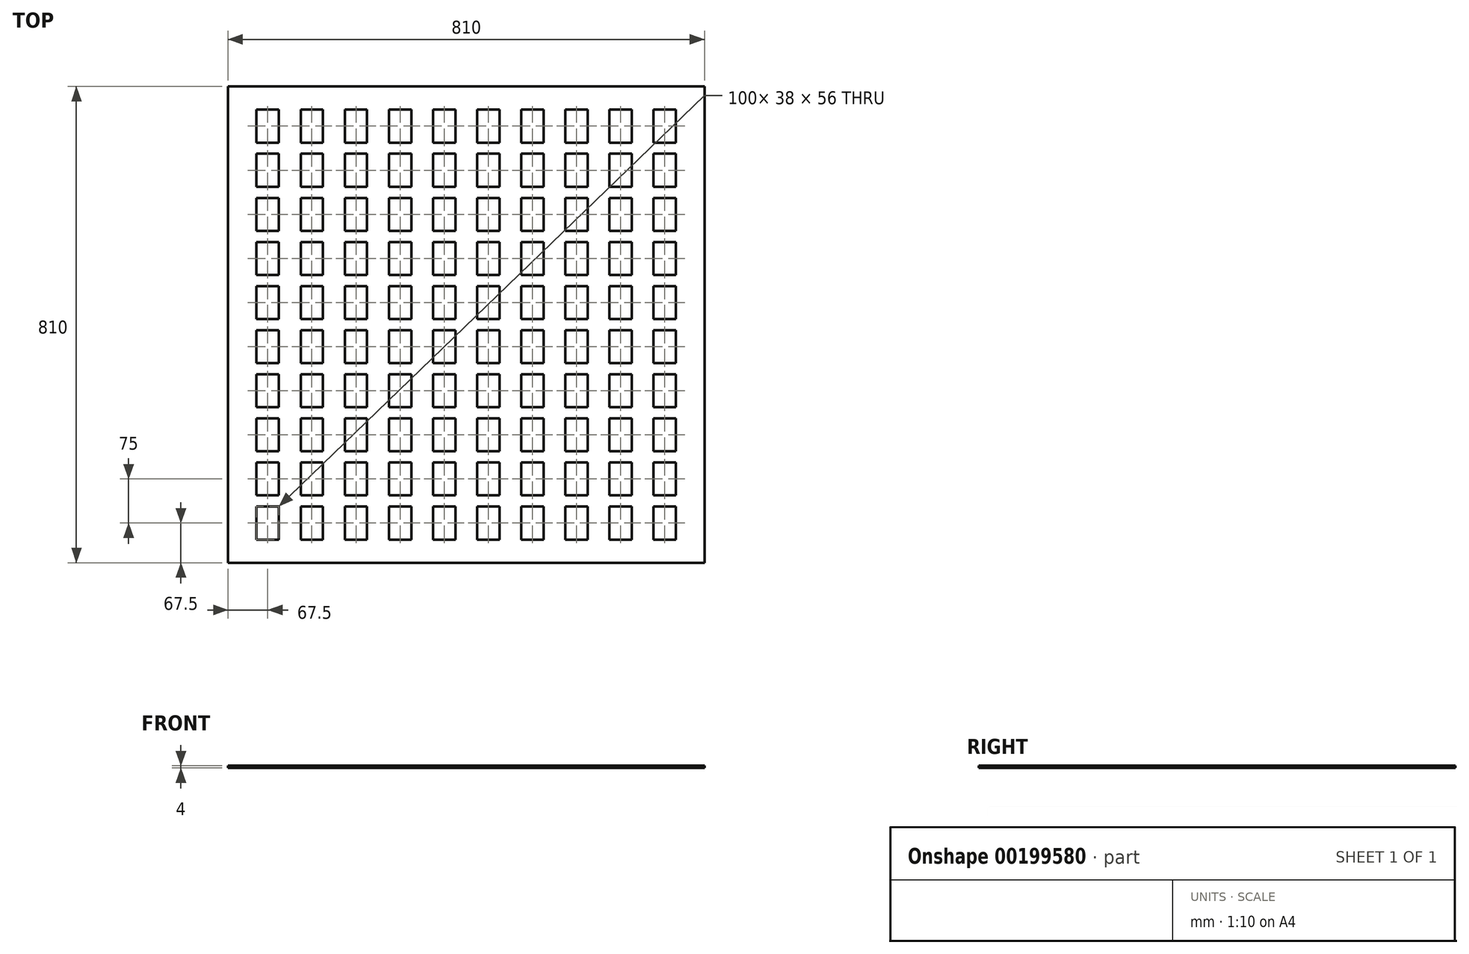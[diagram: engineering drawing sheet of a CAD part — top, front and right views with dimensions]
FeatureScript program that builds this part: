
annotation { "Feature Type Name" : "Feature", "Feature Type Description" : "" }
export const myFeature = defineFeature(function(context is Context, id is Id, definition is map)
    precondition{}
    {
        {
            var Q0;
            Q0=qCreatedBy(makeId("Top.planeOp"),FACE);
            var sketch = newSketch(context, id + "F0", { "sketchPlane" : qUnion([Q0])});
            skLineSegment(sketch, "E0.bottom", {"start": v(-405, 405) * mm, "end": v(405, 405) * mm});
            skLineSegment(sketch, "E0.top", {"start": v(-405, -405) * mm, "end": v(405, -405) * mm});
            skLineSegment(sketch, "E0.left", {"start": v(-405, 405) * mm, "end": v(-405, -405) * mm});
            skLineSegment(sketch, "E0.right", {"start": v(405, 405) * mm, "end": v(405, -405) * mm});
            skSolve(sketch);
        }
        {
            var Q0;
            Q0=makeQuery(id+"F0.imprint","IMPRINT",FACE,{"disambiguationData":[TD([[makeQuery(id+"F0.imprint","IMPRINT",EDGE,{"derivedFrom":sQuery(id+"F0.wireOp",EDGE,"E0.bottom")}),-1.0]])]});
            extrude(context, id + "F1", {"entities" : qUnion([Q0]), "depth" : 4 * mm});
        }
        {
            var Q0;
            Q0=makeQuery(id+"F1.opExtrude","CAP_FACE",FACE,{"disambiguationData":[OSD([sQuery(id+"F0.wireOp",EDGE,"E0.bottom"),sQuery(id+"F0.wireOp",EDGE,"E0.top"),sQuery(id+"F0.wireOp",EDGE,"E0.left"),sQuery(id+"F0.wireOp",EDGE,"E0.right")])],"isStart":false});
            var sketch = newSketch(context, id + "F2", { "sketchPlane" : qUnion([Q0])});
            skCircle(sketch, "E1", {"center": v(-337.5, 337.5) * mm, "radius": 37.5 * mm, "construction": true});
            skLineSegment(sketch, "E2.bottom", {"start": v(-318.5, 309.5) * mm, "end": v(-356.5, 309.5) * mm});
            skLineSegment(sketch, "E2.top", {"start": v(-318.5, 365.5) * mm, "end": v(-356.5, 365.5) * mm});
            skLineSegment(sketch, "E2.left", {"start": v(-318.5, 309.5) * mm, "end": v(-318.5, 365.5) * mm});
            skLineSegment(sketch, "E2.right", {"start": v(-356.5, 309.5) * mm, "end": v(-356.5, 365.5) * mm});
            skLineSegment(sketch, "E3.0.1.0", {"start": v(-318.5, 234.5) * mm, "end": v(-318.5, 290.5) * mm});
            skPoint(sketch, "E3.0.1.1", {"position": v(-337.5, 262.5) * mm});
            skLineSegment(sketch, "E3.0.1.2", {"start": v(-356.5, 234.5) * mm, "end": v(-356.5, 290.5) * mm});
            skCircle(sketch, "E3.0.1.3", {"center": v(-337.5, 262.5) * mm, "radius": 37.5 * mm, "construction": true});
            skLineSegment(sketch, "E3.0.1.4", {"start": v(-318.5, 234.5) * mm, "end": v(-356.5, 234.5) * mm});
            skLineSegment(sketch, "E3.0.1.5", {"start": v(-318.5, 290.5) * mm, "end": v(-356.5, 290.5) * mm});
            skLineSegment(sketch, "E3.0.2.0", {"start": v(-318.5, 159.5) * mm, "end": v(-318.5, 215.5) * mm});
            skPoint(sketch, "E3.0.2.1", {"position": v(-337.5, 187.5) * mm});
            skLineSegment(sketch, "E3.0.2.2", {"start": v(-356.5, 159.5) * mm, "end": v(-356.5, 215.5) * mm});
            skCircle(sketch, "E3.0.2.3", {"center": v(-337.5, 187.5) * mm, "radius": 37.5 * mm, "construction": true});
            skLineSegment(sketch, "E3.0.2.4", {"start": v(-318.5, 159.5) * mm, "end": v(-356.5, 159.5) * mm});
            skLineSegment(sketch, "E3.0.2.5", {"start": v(-318.5, 215.5) * mm, "end": v(-356.5, 215.5) * mm});
            skLineSegment(sketch, "E3.0.3.0", {"start": v(-318.5, 84.5) * mm, "end": v(-318.5, 140.5) * mm});
            skPoint(sketch, "E3.0.3.1", {"position": v(-337.5, 112.5) * mm});
            skLineSegment(sketch, "E3.0.3.2", {"start": v(-356.5, 84.5) * mm, "end": v(-356.5, 140.5) * mm});
            skCircle(sketch, "E3.0.3.3", {"center": v(-337.5, 112.5) * mm, "radius": 37.5 * mm, "construction": true});
            skLineSegment(sketch, "E3.0.3.4", {"start": v(-318.5, 84.5) * mm, "end": v(-356.5, 84.5) * mm});
            skLineSegment(sketch, "E3.0.3.5", {"start": v(-318.5, 140.5) * mm, "end": v(-356.5, 140.5) * mm});
            skLineSegment(sketch, "E3.0.4.0", {"start": v(-318.5, 9.5) * mm, "end": v(-318.5, 65.5) * mm});
            skPoint(sketch, "E3.0.4.1", {"position": v(-337.5, 37.5) * mm});
            skLineSegment(sketch, "E3.0.4.2", {"start": v(-356.5, 9.5) * mm, "end": v(-356.5, 65.5) * mm});
            skCircle(sketch, "E3.0.4.3", {"center": v(-337.5, 37.5) * mm, "radius": 37.5 * mm, "construction": true});
            skLineSegment(sketch, "E3.0.4.4", {"start": v(-318.5, 9.5) * mm, "end": v(-356.5, 9.5) * mm});
            skLineSegment(sketch, "E3.0.4.5", {"start": v(-318.5, 65.5) * mm, "end": v(-356.5, 65.5) * mm});
            skLineSegment(sketch, "E3.0.5.0", {"start": v(-318.5, -65.5) * mm, "end": v(-318.5, -9.5) * mm});
            skPoint(sketch, "E3.0.5.1", {"position": v(-337.5, -37.5) * mm});
            skLineSegment(sketch, "E3.0.5.2", {"start": v(-356.5, -65.5) * mm, "end": v(-356.5, -9.5) * mm});
            skCircle(sketch, "E3.0.5.3", {"center": v(-337.5, -37.5) * mm, "radius": 37.5 * mm, "construction": true});
            skLineSegment(sketch, "E3.0.5.4", {"start": v(-318.5, -65.5) * mm, "end": v(-356.5, -65.5) * mm});
            skLineSegment(sketch, "E3.0.5.5", {"start": v(-318.5, -9.5) * mm, "end": v(-356.5, -9.5) * mm});
            skLineSegment(sketch, "E3.0.6.0", {"start": v(-318.5, -140.5) * mm, "end": v(-318.5, -84.5) * mm});
            skPoint(sketch, "E3.0.6.1", {"position": v(-337.5, -112.5) * mm});
            skLineSegment(sketch, "E3.0.6.2", {"start": v(-356.5, -140.5) * mm, "end": v(-356.5, -84.5) * mm});
            skCircle(sketch, "E3.0.6.3", {"center": v(-337.5, -112.5) * mm, "radius": 37.5 * mm, "construction": true});
            skLineSegment(sketch, "E3.0.6.4", {"start": v(-318.5, -140.5) * mm, "end": v(-356.5, -140.5) * mm});
            skLineSegment(sketch, "E3.0.6.5", {"start": v(-318.5, -84.5) * mm, "end": v(-356.5, -84.5) * mm});
            skLineSegment(sketch, "E3.0.7.0", {"start": v(-318.5, -215.5) * mm, "end": v(-318.5, -159.5) * mm});
            skPoint(sketch, "E3.0.7.1", {"position": v(-337.5, -187.5) * mm});
            skLineSegment(sketch, "E3.0.7.2", {"start": v(-356.5, -215.5) * mm, "end": v(-356.5, -159.5) * mm});
            skCircle(sketch, "E3.0.7.3", {"center": v(-337.5, -187.5) * mm, "radius": 37.5 * mm, "construction": true});
            skLineSegment(sketch, "E3.0.7.4", {"start": v(-318.5, -215.5) * mm, "end": v(-356.5, -215.5) * mm});
            skLineSegment(sketch, "E3.0.7.5", {"start": v(-318.5, -159.5) * mm, "end": v(-356.5, -159.5) * mm});
            skLineSegment(sketch, "E3.0.8.0", {"start": v(-318.5, -290.5) * mm, "end": v(-318.5, -234.5) * mm});
            skPoint(sketch, "E3.0.8.1", {"position": v(-337.5, -262.5) * mm});
            skLineSegment(sketch, "E3.0.8.2", {"start": v(-356.5, -290.5) * mm, "end": v(-356.5, -234.5) * mm});
            skCircle(sketch, "E3.0.8.3", {"center": v(-337.5, -262.5) * mm, "radius": 37.5 * mm, "construction": true});
            skLineSegment(sketch, "E3.0.8.4", {"start": v(-318.5, -290.5) * mm, "end": v(-356.5, -290.5) * mm});
            skLineSegment(sketch, "E3.0.8.5", {"start": v(-318.5, -234.5) * mm, "end": v(-356.5, -234.5) * mm});
            skLineSegment(sketch, "E3.0.9.0", {"start": v(-318.5, -365.5) * mm, "end": v(-318.5, -309.5) * mm});
            skPoint(sketch, "E3.0.9.1", {"position": v(-337.5, -337.5) * mm});
            skLineSegment(sketch, "E3.0.9.2", {"start": v(-356.5, -365.5) * mm, "end": v(-356.5, -309.5) * mm});
            skCircle(sketch, "E3.0.9.3", {"center": v(-337.5, -337.5) * mm, "radius": 37.5 * mm, "construction": true});
            skLineSegment(sketch, "E3.0.9.4", {"start": v(-318.5, -365.5) * mm, "end": v(-356.5, -365.5) * mm});
            skLineSegment(sketch, "E3.0.9.5", {"start": v(-318.5, -309.5) * mm, "end": v(-356.5, -309.5) * mm});
            skLineSegment(sketch, "E3.1.0.0", {"start": v(-243.5, 309.5) * mm, "end": v(-243.5, 365.5) * mm});
            skPoint(sketch, "E3.1.0.1", {"position": v(-262.5, 337.5) * mm});
            skLineSegment(sketch, "E3.1.0.2", {"start": v(-281.5, 309.5) * mm, "end": v(-281.5, 365.5) * mm});
            skCircle(sketch, "E3.1.0.3", {"center": v(-262.5, 337.5) * mm, "radius": 37.5 * mm, "construction": true});
            skLineSegment(sketch, "E3.1.0.4", {"start": v(-243.5, 309.5) * mm, "end": v(-281.5, 309.5) * mm});
            skLineSegment(sketch, "E3.1.0.5", {"start": v(-243.5, 365.5) * mm, "end": v(-281.5, 365.5) * mm});
            skLineSegment(sketch, "E3.1.1.0", {"start": v(-243.5, 234.5) * mm, "end": v(-243.5, 290.5) * mm});
            skPoint(sketch, "E3.1.1.1", {"position": v(-262.5, 262.5) * mm});
            skLineSegment(sketch, "E3.1.1.2", {"start": v(-281.5, 234.5) * mm, "end": v(-281.5, 290.5) * mm});
            skCircle(sketch, "E3.1.1.3", {"center": v(-262.5, 262.5) * mm, "radius": 37.5 * mm, "construction": true});
            skLineSegment(sketch, "E3.1.1.4", {"start": v(-243.5, 234.5) * mm, "end": v(-281.5, 234.5) * mm});
            skLineSegment(sketch, "E3.1.1.5", {"start": v(-243.5, 290.5) * mm, "end": v(-281.5, 290.5) * mm});
            skLineSegment(sketch, "E3.1.2.0", {"start": v(-243.5, 159.5) * mm, "end": v(-243.5, 215.5) * mm});
            skPoint(sketch, "E3.1.2.1", {"position": v(-262.5, 187.5) * mm});
            skLineSegment(sketch, "E3.1.2.2", {"start": v(-281.5, 159.5) * mm, "end": v(-281.5, 215.5) * mm});
            skCircle(sketch, "E3.1.2.3", {"center": v(-262.5, 187.5) * mm, "radius": 37.5 * mm, "construction": true});
            skLineSegment(sketch, "E3.1.2.4", {"start": v(-243.5, 159.5) * mm, "end": v(-281.5, 159.5) * mm});
            skLineSegment(sketch, "E3.1.2.5", {"start": v(-243.5, 215.5) * mm, "end": v(-281.5, 215.5) * mm});
            skLineSegment(sketch, "E3.1.3.0", {"start": v(-243.5, 84.5) * mm, "end": v(-243.5, 140.5) * mm});
            skPoint(sketch, "E3.1.3.1", {"position": v(-262.5, 112.5) * mm});
            skLineSegment(sketch, "E3.1.3.2", {"start": v(-281.5, 84.5) * mm, "end": v(-281.5, 140.5) * mm});
            skCircle(sketch, "E3.1.3.3", {"center": v(-262.5, 112.5) * mm, "radius": 37.5 * mm, "construction": true});
            skLineSegment(sketch, "E3.1.3.4", {"start": v(-243.5, 84.5) * mm, "end": v(-281.5, 84.5) * mm});
            skLineSegment(sketch, "E3.1.3.5", {"start": v(-243.5, 140.5) * mm, "end": v(-281.5, 140.5) * mm});
            skLineSegment(sketch, "E3.1.4.0", {"start": v(-243.5, 9.5) * mm, "end": v(-243.5, 65.5) * mm});
            skPoint(sketch, "E3.1.4.1", {"position": v(-262.5, 37.5) * mm});
            skLineSegment(sketch, "E3.1.4.2", {"start": v(-281.5, 9.5) * mm, "end": v(-281.5, 65.5) * mm});
            skCircle(sketch, "E3.1.4.3", {"center": v(-262.5, 37.5) * mm, "radius": 37.5 * mm, "construction": true});
            skLineSegment(sketch, "E3.1.4.4", {"start": v(-243.5, 9.5) * mm, "end": v(-281.5, 9.5) * mm});
            skLineSegment(sketch, "E3.1.4.5", {"start": v(-243.5, 65.5) * mm, "end": v(-281.5, 65.5) * mm});
            skLineSegment(sketch, "E3.1.5.0", {"start": v(-243.5, -65.5) * mm, "end": v(-243.5, -9.5) * mm});
            skPoint(sketch, "E3.1.5.1", {"position": v(-262.5, -37.5) * mm});
            skLineSegment(sketch, "E3.1.5.2", {"start": v(-281.5, -65.5) * mm, "end": v(-281.5, -9.5) * mm});
            skCircle(sketch, "E3.1.5.3", {"center": v(-262.5, -37.5) * mm, "radius": 37.5 * mm, "construction": true});
            skLineSegment(sketch, "E3.1.5.4", {"start": v(-243.5, -65.5) * mm, "end": v(-281.5, -65.5) * mm});
            skLineSegment(sketch, "E3.1.5.5", {"start": v(-243.5, -9.5) * mm, "end": v(-281.5, -9.5) * mm});
            skLineSegment(sketch, "E3.1.6.0", {"start": v(-243.5, -140.5) * mm, "end": v(-243.5, -84.5) * mm});
            skPoint(sketch, "E3.1.6.1", {"position": v(-262.5, -112.5) * mm});
            skLineSegment(sketch, "E3.1.6.2", {"start": v(-281.5, -140.5) * mm, "end": v(-281.5, -84.5) * mm});
            skCircle(sketch, "E3.1.6.3", {"center": v(-262.5, -112.5) * mm, "radius": 37.5 * mm, "construction": true});
            skLineSegment(sketch, "E3.1.6.4", {"start": v(-243.5, -140.5) * mm, "end": v(-281.5, -140.5) * mm});
            skLineSegment(sketch, "E3.1.6.5", {"start": v(-243.5, -84.5) * mm, "end": v(-281.5, -84.5) * mm});
            skLineSegment(sketch, "E3.1.7.0", {"start": v(-243.5, -215.5) * mm, "end": v(-243.5, -159.5) * mm});
            skPoint(sketch, "E3.1.7.1", {"position": v(-262.5, -187.5) * mm});
            skLineSegment(sketch, "E3.1.7.2", {"start": v(-281.5, -215.5) * mm, "end": v(-281.5, -159.5) * mm});
            skCircle(sketch, "E3.1.7.3", {"center": v(-262.5, -187.5) * mm, "radius": 37.5 * mm, "construction": true});
            skLineSegment(sketch, "E3.1.7.4", {"start": v(-243.5, -215.5) * mm, "end": v(-281.5, -215.5) * mm});
            skLineSegment(sketch, "E3.1.7.5", {"start": v(-243.5, -159.5) * mm, "end": v(-281.5, -159.5) * mm});
            skLineSegment(sketch, "E3.1.8.0", {"start": v(-243.5, -290.5) * mm, "end": v(-243.5, -234.5) * mm});
            skPoint(sketch, "E3.1.8.1", {"position": v(-262.5, -262.5) * mm});
            skLineSegment(sketch, "E3.1.8.2", {"start": v(-281.5, -290.5) * mm, "end": v(-281.5, -234.5) * mm});
            skCircle(sketch, "E3.1.8.3", {"center": v(-262.5, -262.5) * mm, "radius": 37.5 * mm, "construction": true});
            skLineSegment(sketch, "E3.1.8.4", {"start": v(-243.5, -290.5) * mm, "end": v(-281.5, -290.5) * mm});
            skLineSegment(sketch, "E3.1.8.5", {"start": v(-243.5, -234.5) * mm, "end": v(-281.5, -234.5) * mm});
            skLineSegment(sketch, "E3.1.9.0", {"start": v(-243.5, -365.5) * mm, "end": v(-243.5, -309.5) * mm});
            skPoint(sketch, "E3.1.9.1", {"position": v(-262.5, -337.5) * mm});
            skLineSegment(sketch, "E3.1.9.2", {"start": v(-281.5, -365.5) * mm, "end": v(-281.5, -309.5) * mm});
            skCircle(sketch, "E3.1.9.3", {"center": v(-262.5, -337.5) * mm, "radius": 37.5 * mm, "construction": true});
            skLineSegment(sketch, "E3.1.9.4", {"start": v(-243.5, -365.5) * mm, "end": v(-281.5, -365.5) * mm});
            skLineSegment(sketch, "E3.1.9.5", {"start": v(-243.5, -309.5) * mm, "end": v(-281.5, -309.5) * mm});
            skLineSegment(sketch, "E3.2.0.0", {"start": v(-168.5, 309.5) * mm, "end": v(-168.5, 365.5) * mm});
            skPoint(sketch, "E3.2.0.1", {"position": v(-187.5, 337.5) * mm});
            skLineSegment(sketch, "E3.2.0.2", {"start": v(-206.5, 309.5) * mm, "end": v(-206.5, 365.5) * mm});
            skCircle(sketch, "E3.2.0.3", {"center": v(-187.5, 337.5) * mm, "radius": 37.5 * mm, "construction": true});
            skLineSegment(sketch, "E3.2.0.4", {"start": v(-168.5, 309.5) * mm, "end": v(-206.5, 309.5) * mm});
            skLineSegment(sketch, "E3.2.0.5", {"start": v(-168.5, 365.5) * mm, "end": v(-206.5, 365.5) * mm});
            skLineSegment(sketch, "E3.2.1.0", {"start": v(-168.5, 234.5) * mm, "end": v(-168.5, 290.5) * mm});
            skPoint(sketch, "E3.2.1.1", {"position": v(-187.5, 262.5) * mm});
            skLineSegment(sketch, "E3.2.1.2", {"start": v(-206.5, 234.5) * mm, "end": v(-206.5, 290.5) * mm});
            skCircle(sketch, "E3.2.1.3", {"center": v(-187.5, 262.5) * mm, "radius": 37.5 * mm, "construction": true});
            skLineSegment(sketch, "E3.2.1.4", {"start": v(-168.5, 234.5) * mm, "end": v(-206.5, 234.5) * mm});
            skLineSegment(sketch, "E3.2.1.5", {"start": v(-168.5, 290.5) * mm, "end": v(-206.5, 290.5) * mm});
            skLineSegment(sketch, "E3.2.2.0", {"start": v(-168.5, 159.5) * mm, "end": v(-168.5, 215.5) * mm});
            skPoint(sketch, "E3.2.2.1", {"position": v(-187.5, 187.5) * mm});
            skLineSegment(sketch, "E3.2.2.2", {"start": v(-206.5, 159.5) * mm, "end": v(-206.5, 215.5) * mm});
            skCircle(sketch, "E3.2.2.3", {"center": v(-187.5, 187.5) * mm, "radius": 37.5 * mm, "construction": true});
            skLineSegment(sketch, "E3.2.2.4", {"start": v(-168.5, 159.5) * mm, "end": v(-206.5, 159.5) * mm});
            skLineSegment(sketch, "E3.2.2.5", {"start": v(-168.5, 215.5) * mm, "end": v(-206.5, 215.5) * mm});
            skLineSegment(sketch, "E3.2.3.0", {"start": v(-168.5, 84.5) * mm, "end": v(-168.5, 140.5) * mm});
            skPoint(sketch, "E3.2.3.1", {"position": v(-187.5, 112.5) * mm});
            skLineSegment(sketch, "E3.2.3.2", {"start": v(-206.5, 84.5) * mm, "end": v(-206.5, 140.5) * mm});
            skCircle(sketch, "E3.2.3.3", {"center": v(-187.5, 112.5) * mm, "radius": 37.5 * mm, "construction": true});
            skLineSegment(sketch, "E3.2.3.4", {"start": v(-168.5, 84.5) * mm, "end": v(-206.5, 84.5) * mm});
            skLineSegment(sketch, "E3.2.3.5", {"start": v(-168.5, 140.5) * mm, "end": v(-206.5, 140.5) * mm});
            skLineSegment(sketch, "E3.2.4.0", {"start": v(-168.5, 9.5) * mm, "end": v(-168.5, 65.5) * mm});
            skPoint(sketch, "E3.2.4.1", {"position": v(-187.5, 37.5) * mm});
            skLineSegment(sketch, "E3.2.4.2", {"start": v(-206.5, 9.5) * mm, "end": v(-206.5, 65.5) * mm});
            skCircle(sketch, "E3.2.4.3", {"center": v(-187.5, 37.5) * mm, "radius": 37.5 * mm, "construction": true});
            skLineSegment(sketch, "E3.2.4.4", {"start": v(-168.5, 9.5) * mm, "end": v(-206.5, 9.5) * mm});
            skLineSegment(sketch, "E3.2.4.5", {"start": v(-168.5, 65.5) * mm, "end": v(-206.5, 65.5) * mm});
            skLineSegment(sketch, "E3.2.5.0", {"start": v(-168.5, -65.5) * mm, "end": v(-168.5, -9.5) * mm});
            skPoint(sketch, "E3.2.5.1", {"position": v(-187.5, -37.5) * mm});
            skLineSegment(sketch, "E3.2.5.2", {"start": v(-206.5, -65.5) * mm, "end": v(-206.5, -9.5) * mm});
            skCircle(sketch, "E3.2.5.3", {"center": v(-187.5, -37.5) * mm, "radius": 37.5 * mm, "construction": true});
            skLineSegment(sketch, "E3.2.5.4", {"start": v(-168.5, -65.5) * mm, "end": v(-206.5, -65.5) * mm});
            skLineSegment(sketch, "E3.2.5.5", {"start": v(-168.5, -9.5) * mm, "end": v(-206.5, -9.5) * mm});
            skLineSegment(sketch, "E3.2.6.0", {"start": v(-168.5, -140.5) * mm, "end": v(-168.5, -84.5) * mm});
            skPoint(sketch, "E3.2.6.1", {"position": v(-187.5, -112.5) * mm});
            skLineSegment(sketch, "E3.2.6.2", {"start": v(-206.5, -140.5) * mm, "end": v(-206.5, -84.5) * mm});
            skCircle(sketch, "E3.2.6.3", {"center": v(-187.5, -112.5) * mm, "radius": 37.5 * mm, "construction": true});
            skLineSegment(sketch, "E3.2.6.4", {"start": v(-168.5, -140.5) * mm, "end": v(-206.5, -140.5) * mm});
            skLineSegment(sketch, "E3.2.6.5", {"start": v(-168.5, -84.5) * mm, "end": v(-206.5, -84.5) * mm});
            skLineSegment(sketch, "E3.2.7.0", {"start": v(-168.5, -215.5) * mm, "end": v(-168.5, -159.5) * mm});
            skPoint(sketch, "E3.2.7.1", {"position": v(-187.5, -187.5) * mm});
            skLineSegment(sketch, "E3.2.7.2", {"start": v(-206.5, -215.5) * mm, "end": v(-206.5, -159.5) * mm});
            skCircle(sketch, "E3.2.7.3", {"center": v(-187.5, -187.5) * mm, "radius": 37.5 * mm, "construction": true});
            skLineSegment(sketch, "E3.2.7.4", {"start": v(-168.5, -215.5) * mm, "end": v(-206.5, -215.5) * mm});
            skLineSegment(sketch, "E3.2.7.5", {"start": v(-168.5, -159.5) * mm, "end": v(-206.5, -159.5) * mm});
            skLineSegment(sketch, "E3.2.8.0", {"start": v(-168.5, -290.5) * mm, "end": v(-168.5, -234.5) * mm});
            skPoint(sketch, "E3.2.8.1", {"position": v(-187.5, -262.5) * mm});
            skLineSegment(sketch, "E3.2.8.2", {"start": v(-206.5, -290.5) * mm, "end": v(-206.5, -234.5) * mm});
            skCircle(sketch, "E3.2.8.3", {"center": v(-187.5, -262.5) * mm, "radius": 37.5 * mm, "construction": true});
            skLineSegment(sketch, "E3.2.8.4", {"start": v(-168.5, -290.5) * mm, "end": v(-206.5, -290.5) * mm});
            skLineSegment(sketch, "E3.2.8.5", {"start": v(-168.5, -234.5) * mm, "end": v(-206.5, -234.5) * mm});
            skLineSegment(sketch, "E3.2.9.0", {"start": v(-168.5, -365.5) * mm, "end": v(-168.5, -309.5) * mm});
            skPoint(sketch, "E3.2.9.1", {"position": v(-187.5, -337.5) * mm});
            skLineSegment(sketch, "E3.2.9.2", {"start": v(-206.5, -365.5) * mm, "end": v(-206.5, -309.5) * mm});
            skCircle(sketch, "E3.2.9.3", {"center": v(-187.5, -337.5) * mm, "radius": 37.5 * mm, "construction": true});
            skLineSegment(sketch, "E3.2.9.4", {"start": v(-168.5, -365.5) * mm, "end": v(-206.5, -365.5) * mm});
            skLineSegment(sketch, "E3.2.9.5", {"start": v(-168.5, -309.5) * mm, "end": v(-206.5, -309.5) * mm});
            skLineSegment(sketch, "E3.3.0.0", {"start": v(-93.5, 309.5) * mm, "end": v(-93.5, 365.5) * mm});
            skPoint(sketch, "E3.3.0.1", {"position": v(-112.5, 337.5) * mm});
            skLineSegment(sketch, "E3.3.0.2", {"start": v(-131.5, 309.5) * mm, "end": v(-131.5, 365.5) * mm});
            skCircle(sketch, "E3.3.0.3", {"center": v(-112.5, 337.5) * mm, "radius": 37.5 * mm, "construction": true});
            skLineSegment(sketch, "E3.3.0.4", {"start": v(-93.5, 309.5) * mm, "end": v(-131.5, 309.5) * mm});
            skLineSegment(sketch, "E3.3.0.5", {"start": v(-93.5, 365.5) * mm, "end": v(-131.5, 365.5) * mm});
            skLineSegment(sketch, "E3.3.1.0", {"start": v(-93.5, 234.5) * mm, "end": v(-93.5, 290.5) * mm});
            skPoint(sketch, "E3.3.1.1", {"position": v(-112.5, 262.5) * mm});
            skLineSegment(sketch, "E3.3.1.2", {"start": v(-131.5, 234.5) * mm, "end": v(-131.5, 290.5) * mm});
            skCircle(sketch, "E3.3.1.3", {"center": v(-112.5, 262.5) * mm, "radius": 37.5 * mm, "construction": true});
            skLineSegment(sketch, "E3.3.1.4", {"start": v(-93.5, 234.5) * mm, "end": v(-131.5, 234.5) * mm});
            skLineSegment(sketch, "E3.3.1.5", {"start": v(-93.5, 290.5) * mm, "end": v(-131.5, 290.5) * mm});
            skLineSegment(sketch, "E3.3.2.0", {"start": v(-93.5, 159.5) * mm, "end": v(-93.5, 215.5) * mm});
            skPoint(sketch, "E3.3.2.1", {"position": v(-112.5, 187.5) * mm});
            skLineSegment(sketch, "E3.3.2.2", {"start": v(-131.5, 159.5) * mm, "end": v(-131.5, 215.5) * mm});
            skCircle(sketch, "E3.3.2.3", {"center": v(-112.5, 187.5) * mm, "radius": 37.5 * mm, "construction": true});
            skLineSegment(sketch, "E3.3.2.4", {"start": v(-93.5, 159.5) * mm, "end": v(-131.5, 159.5) * mm});
            skLineSegment(sketch, "E3.3.2.5", {"start": v(-93.5, 215.5) * mm, "end": v(-131.5, 215.5) * mm});
            skLineSegment(sketch, "E3.3.3.0", {"start": v(-93.5, 84.5) * mm, "end": v(-93.5, 140.5) * mm});
            skPoint(sketch, "E3.3.3.1", {"position": v(-112.5, 112.5) * mm});
            skLineSegment(sketch, "E3.3.3.2", {"start": v(-131.5, 84.5) * mm, "end": v(-131.5, 140.5) * mm});
            skCircle(sketch, "E3.3.3.3", {"center": v(-112.5, 112.5) * mm, "radius": 37.5 * mm, "construction": true});
            skLineSegment(sketch, "E3.3.3.4", {"start": v(-93.5, 84.5) * mm, "end": v(-131.5, 84.5) * mm});
            skLineSegment(sketch, "E3.3.3.5", {"start": v(-93.5, 140.5) * mm, "end": v(-131.5, 140.5) * mm});
            skLineSegment(sketch, "E3.3.4.0", {"start": v(-93.5, 9.5) * mm, "end": v(-93.5, 65.5) * mm});
            skPoint(sketch, "E3.3.4.1", {"position": v(-112.5, 37.5) * mm});
            skLineSegment(sketch, "E3.3.4.2", {"start": v(-131.5, 9.5) * mm, "end": v(-131.5, 65.5) * mm});
            skCircle(sketch, "E3.3.4.3", {"center": v(-112.5, 37.5) * mm, "radius": 37.5 * mm, "construction": true});
            skLineSegment(sketch, "E3.3.4.4", {"start": v(-93.5, 9.5) * mm, "end": v(-131.5, 9.5) * mm});
            skLineSegment(sketch, "E3.3.4.5", {"start": v(-93.5, 65.5) * mm, "end": v(-131.5, 65.5) * mm});
            skLineSegment(sketch, "E3.3.5.0", {"start": v(-93.5, -65.5) * mm, "end": v(-93.5, -9.5) * mm});
            skPoint(sketch, "E3.3.5.1", {"position": v(-112.5, -37.5) * mm});
            skLineSegment(sketch, "E3.3.5.2", {"start": v(-131.5, -65.5) * mm, "end": v(-131.5, -9.5) * mm});
            skCircle(sketch, "E3.3.5.3", {"center": v(-112.5, -37.5) * mm, "radius": 37.5 * mm, "construction": true});
            skLineSegment(sketch, "E3.3.5.4", {"start": v(-93.5, -65.5) * mm, "end": v(-131.5, -65.5) * mm});
            skLineSegment(sketch, "E3.3.5.5", {"start": v(-93.5, -9.5) * mm, "end": v(-131.5, -9.5) * mm});
            skLineSegment(sketch, "E3.3.6.0", {"start": v(-93.5, -140.5) * mm, "end": v(-93.5, -84.5) * mm});
            skPoint(sketch, "E3.3.6.1", {"position": v(-112.5, -112.5) * mm});
            skLineSegment(sketch, "E3.3.6.2", {"start": v(-131.5, -140.5) * mm, "end": v(-131.5, -84.5) * mm});
            skCircle(sketch, "E3.3.6.3", {"center": v(-112.5, -112.5) * mm, "radius": 37.5 * mm, "construction": true});
            skLineSegment(sketch, "E3.3.6.4", {"start": v(-93.5, -140.5) * mm, "end": v(-131.5, -140.5) * mm});
            skLineSegment(sketch, "E3.3.6.5", {"start": v(-93.5, -84.5) * mm, "end": v(-131.5, -84.5) * mm});
            skLineSegment(sketch, "E3.3.7.0", {"start": v(-93.5, -215.5) * mm, "end": v(-93.5, -159.5) * mm});
            skPoint(sketch, "E3.3.7.1", {"position": v(-112.5, -187.5) * mm});
            skLineSegment(sketch, "E3.3.7.2", {"start": v(-131.5, -215.5) * mm, "end": v(-131.5, -159.5) * mm});
            skCircle(sketch, "E3.3.7.3", {"center": v(-112.5, -187.5) * mm, "radius": 37.5 * mm, "construction": true});
            skLineSegment(sketch, "E3.3.7.4", {"start": v(-93.5, -215.5) * mm, "end": v(-131.5, -215.5) * mm});
            skLineSegment(sketch, "E3.3.7.5", {"start": v(-93.5, -159.5) * mm, "end": v(-131.5, -159.5) * mm});
            skLineSegment(sketch, "E3.3.8.0", {"start": v(-93.5, -290.5) * mm, "end": v(-93.5, -234.5) * mm});
            skPoint(sketch, "E3.3.8.1", {"position": v(-112.5, -262.5) * mm});
            skLineSegment(sketch, "E3.3.8.2", {"start": v(-131.5, -290.5) * mm, "end": v(-131.5, -234.5) * mm});
            skCircle(sketch, "E3.3.8.3", {"center": v(-112.5, -262.5) * mm, "radius": 37.5 * mm, "construction": true});
            skLineSegment(sketch, "E3.3.8.4", {"start": v(-93.5, -290.5) * mm, "end": v(-131.5, -290.5) * mm});
            skLineSegment(sketch, "E3.3.8.5", {"start": v(-93.5, -234.5) * mm, "end": v(-131.5, -234.5) * mm});
            skLineSegment(sketch, "E3.3.9.0", {"start": v(-93.5, -365.5) * mm, "end": v(-93.5, -309.5) * mm});
            skPoint(sketch, "E3.3.9.1", {"position": v(-112.5, -337.5) * mm});
            skLineSegment(sketch, "E3.3.9.2", {"start": v(-131.5, -365.5) * mm, "end": v(-131.5, -309.5) * mm});
            skCircle(sketch, "E3.3.9.3", {"center": v(-112.5, -337.5) * mm, "radius": 37.5 * mm, "construction": true});
            skLineSegment(sketch, "E3.3.9.4", {"start": v(-93.5, -365.5) * mm, "end": v(-131.5, -365.5) * mm});
            skLineSegment(sketch, "E3.3.9.5", {"start": v(-93.5, -309.5) * mm, "end": v(-131.5, -309.5) * mm});
            skLineSegment(sketch, "E3.4.0.0", {"start": v(-18.5, 309.5) * mm, "end": v(-18.5, 365.5) * mm});
            skPoint(sketch, "E3.4.0.1", {"position": v(-37.5, 337.5) * mm});
            skLineSegment(sketch, "E3.4.0.2", {"start": v(-56.5, 309.5) * mm, "end": v(-56.5, 365.5) * mm});
            skCircle(sketch, "E3.4.0.3", {"center": v(-37.5, 337.5) * mm, "radius": 37.5 * mm, "construction": true});
            skLineSegment(sketch, "E3.4.0.4", {"start": v(-18.5, 309.5) * mm, "end": v(-56.5, 309.5) * mm});
            skLineSegment(sketch, "E3.4.0.5", {"start": v(-18.5, 365.5) * mm, "end": v(-56.5, 365.5) * mm});
            skLineSegment(sketch, "E3.4.1.0", {"start": v(-18.5, 234.5) * mm, "end": v(-18.5, 290.5) * mm});
            skPoint(sketch, "E3.4.1.1", {"position": v(-37.5, 262.5) * mm});
            skLineSegment(sketch, "E3.4.1.2", {"start": v(-56.5, 234.5) * mm, "end": v(-56.5, 290.5) * mm});
            skCircle(sketch, "E3.4.1.3", {"center": v(-37.5, 262.5) * mm, "radius": 37.5 * mm, "construction": true});
            skLineSegment(sketch, "E3.4.1.4", {"start": v(-18.5, 234.5) * mm, "end": v(-56.5, 234.5) * mm});
            skLineSegment(sketch, "E3.4.1.5", {"start": v(-18.5, 290.5) * mm, "end": v(-56.5, 290.5) * mm});
            skLineSegment(sketch, "E3.4.2.0", {"start": v(-18.5, 159.5) * mm, "end": v(-18.5, 215.5) * mm});
            skPoint(sketch, "E3.4.2.1", {"position": v(-37.5, 187.5) * mm});
            skLineSegment(sketch, "E3.4.2.2", {"start": v(-56.5, 159.5) * mm, "end": v(-56.5, 215.5) * mm});
            skCircle(sketch, "E3.4.2.3", {"center": v(-37.5, 187.5) * mm, "radius": 37.5 * mm, "construction": true});
            skLineSegment(sketch, "E3.4.2.4", {"start": v(-18.5, 159.5) * mm, "end": v(-56.5, 159.5) * mm});
            skLineSegment(sketch, "E3.4.2.5", {"start": v(-18.5, 215.5) * mm, "end": v(-56.5, 215.5) * mm});
            skLineSegment(sketch, "E3.4.3.0", {"start": v(-18.5, 84.5) * mm, "end": v(-18.5, 140.5) * mm});
            skPoint(sketch, "E3.4.3.1", {"position": v(-37.5, 112.5) * mm});
            skLineSegment(sketch, "E3.4.3.2", {"start": v(-56.5, 84.5) * mm, "end": v(-56.5, 140.5) * mm});
            skCircle(sketch, "E3.4.3.3", {"center": v(-37.5, 112.5) * mm, "radius": 37.5 * mm, "construction": true});
            skLineSegment(sketch, "E3.4.3.4", {"start": v(-18.5, 84.5) * mm, "end": v(-56.5, 84.5) * mm});
            skLineSegment(sketch, "E3.4.3.5", {"start": v(-18.5, 140.5) * mm, "end": v(-56.5, 140.5) * mm});
            skLineSegment(sketch, "E3.4.4.0", {"start": v(-18.5, 9.5) * mm, "end": v(-18.5, 65.5) * mm});
            skPoint(sketch, "E3.4.4.1", {"position": v(-37.5, 37.5) * mm});
            skLineSegment(sketch, "E3.4.4.2", {"start": v(-56.5, 9.5) * mm, "end": v(-56.5, 65.5) * mm});
            skCircle(sketch, "E3.4.4.3", {"center": v(-37.5, 37.5) * mm, "radius": 37.5 * mm, "construction": true});
            skLineSegment(sketch, "E3.4.4.4", {"start": v(-18.5, 9.5) * mm, "end": v(-56.5, 9.5) * mm});
            skLineSegment(sketch, "E3.4.4.5", {"start": v(-18.5, 65.5) * mm, "end": v(-56.5, 65.5) * mm});
            skLineSegment(sketch, "E3.4.5.0", {"start": v(-18.5, -65.5) * mm, "end": v(-18.5, -9.5) * mm});
            skPoint(sketch, "E3.4.5.1", {"position": v(-37.5, -37.5) * mm});
            skLineSegment(sketch, "E3.4.5.2", {"start": v(-56.5, -65.5) * mm, "end": v(-56.5, -9.5) * mm});
            skCircle(sketch, "E3.4.5.3", {"center": v(-37.5, -37.5) * mm, "radius": 37.5 * mm, "construction": true});
            skLineSegment(sketch, "E3.4.5.4", {"start": v(-18.5, -65.5) * mm, "end": v(-56.5, -65.5) * mm});
            skLineSegment(sketch, "E3.4.5.5", {"start": v(-18.5, -9.5) * mm, "end": v(-56.5, -9.5) * mm});
            skLineSegment(sketch, "E3.4.6.0", {"start": v(-18.5, -140.5) * mm, "end": v(-18.5, -84.5) * mm});
            skPoint(sketch, "E3.4.6.1", {"position": v(-37.5, -112.5) * mm});
            skLineSegment(sketch, "E3.4.6.2", {"start": v(-56.5, -140.5) * mm, "end": v(-56.5, -84.5) * mm});
            skCircle(sketch, "E3.4.6.3", {"center": v(-37.5, -112.5) * mm, "radius": 37.5 * mm, "construction": true});
            skLineSegment(sketch, "E3.4.6.4", {"start": v(-18.5, -140.5) * mm, "end": v(-56.5, -140.5) * mm});
            skLineSegment(sketch, "E3.4.6.5", {"start": v(-18.5, -84.5) * mm, "end": v(-56.5, -84.5) * mm});
            skLineSegment(sketch, "E3.4.7.0", {"start": v(-18.5, -215.5) * mm, "end": v(-18.5, -159.5) * mm});
            skPoint(sketch, "E3.4.7.1", {"position": v(-37.5, -187.5) * mm});
            skLineSegment(sketch, "E3.4.7.2", {"start": v(-56.5, -215.5) * mm, "end": v(-56.5, -159.5) * mm});
            skCircle(sketch, "E3.4.7.3", {"center": v(-37.5, -187.5) * mm, "radius": 37.5 * mm, "construction": true});
            skLineSegment(sketch, "E3.4.7.4", {"start": v(-18.5, -215.5) * mm, "end": v(-56.5, -215.5) * mm});
            skLineSegment(sketch, "E3.4.7.5", {"start": v(-18.5, -159.5) * mm, "end": v(-56.5, -159.5) * mm});
            skLineSegment(sketch, "E3.4.8.0", {"start": v(-18.5, -290.5) * mm, "end": v(-18.5, -234.5) * mm});
            skPoint(sketch, "E3.4.8.1", {"position": v(-37.5, -262.5) * mm});
            skLineSegment(sketch, "E3.4.8.2", {"start": v(-56.5, -290.5) * mm, "end": v(-56.5, -234.5) * mm});
            skCircle(sketch, "E3.4.8.3", {"center": v(-37.5, -262.5) * mm, "radius": 37.5 * mm, "construction": true});
            skLineSegment(sketch, "E3.4.8.4", {"start": v(-18.5, -290.5) * mm, "end": v(-56.5, -290.5) * mm});
            skLineSegment(sketch, "E3.4.8.5", {"start": v(-18.5, -234.5) * mm, "end": v(-56.5, -234.5) * mm});
            skLineSegment(sketch, "E3.4.9.0", {"start": v(-18.5, -365.5) * mm, "end": v(-18.5, -309.5) * mm});
            skPoint(sketch, "E3.4.9.1", {"position": v(-37.5, -337.5) * mm});
            skLineSegment(sketch, "E3.4.9.2", {"start": v(-56.5, -365.5) * mm, "end": v(-56.5, -309.5) * mm});
            skCircle(sketch, "E3.4.9.3", {"center": v(-37.5, -337.5) * mm, "radius": 37.5 * mm, "construction": true});
            skLineSegment(sketch, "E3.4.9.4", {"start": v(-18.5, -365.5) * mm, "end": v(-56.5, -365.5) * mm});
            skLineSegment(sketch, "E3.4.9.5", {"start": v(-18.5, -309.5) * mm, "end": v(-56.5, -309.5) * mm});
            skLineSegment(sketch, "E3.5.0.0", {"start": v(56.5, 309.5) * mm, "end": v(56.5, 365.5) * mm});
            skPoint(sketch, "E3.5.0.1", {"position": v(37.5, 337.5) * mm});
            skLineSegment(sketch, "E3.5.0.2", {"start": v(18.5, 309.5) * mm, "end": v(18.5, 365.5) * mm});
            skCircle(sketch, "E3.5.0.3", {"center": v(37.5, 337.5) * mm, "radius": 37.5 * mm, "construction": true});
            skLineSegment(sketch, "E3.5.0.4", {"start": v(56.5, 309.5) * mm, "end": v(18.5, 309.5) * mm});
            skLineSegment(sketch, "E3.5.0.5", {"start": v(56.5, 365.5) * mm, "end": v(18.5, 365.5) * mm});
            skLineSegment(sketch, "E3.5.1.0", {"start": v(56.5, 234.5) * mm, "end": v(56.5, 290.5) * mm});
            skPoint(sketch, "E3.5.1.1", {"position": v(37.5, 262.5) * mm});
            skLineSegment(sketch, "E3.5.1.2", {"start": v(18.5, 234.5) * mm, "end": v(18.5, 290.5) * mm});
            skCircle(sketch, "E3.5.1.3", {"center": v(37.5, 262.5) * mm, "radius": 37.5 * mm, "construction": true});
            skLineSegment(sketch, "E3.5.1.4", {"start": v(56.5, 234.5) * mm, "end": v(18.5, 234.5) * mm});
            skLineSegment(sketch, "E3.5.1.5", {"start": v(56.5, 290.5) * mm, "end": v(18.5, 290.5) * mm});
            skLineSegment(sketch, "E3.5.2.0", {"start": v(56.5, 159.5) * mm, "end": v(56.5, 215.5) * mm});
            skPoint(sketch, "E3.5.2.1", {"position": v(37.5, 187.5) * mm});
            skLineSegment(sketch, "E3.5.2.2", {"start": v(18.5, 159.5) * mm, "end": v(18.5, 215.5) * mm});
            skCircle(sketch, "E3.5.2.3", {"center": v(37.5, 187.5) * mm, "radius": 37.5 * mm, "construction": true});
            skLineSegment(sketch, "E3.5.2.4", {"start": v(56.5, 159.5) * mm, "end": v(18.5, 159.5) * mm});
            skLineSegment(sketch, "E3.5.2.5", {"start": v(56.5, 215.5) * mm, "end": v(18.5, 215.5) * mm});
            skLineSegment(sketch, "E3.5.3.0", {"start": v(56.5, 84.5) * mm, "end": v(56.5, 140.5) * mm});
            skPoint(sketch, "E3.5.3.1", {"position": v(37.5, 112.5) * mm});
            skLineSegment(sketch, "E3.5.3.2", {"start": v(18.5, 84.5) * mm, "end": v(18.5, 140.5) * mm});
            skCircle(sketch, "E3.5.3.3", {"center": v(37.5, 112.5) * mm, "radius": 37.5 * mm, "construction": true});
            skLineSegment(sketch, "E3.5.3.4", {"start": v(56.5, 84.5) * mm, "end": v(18.5, 84.5) * mm});
            skLineSegment(sketch, "E3.5.3.5", {"start": v(56.5, 140.5) * mm, "end": v(18.5, 140.5) * mm});
            skLineSegment(sketch, "E3.5.4.0", {"start": v(56.5, 9.5) * mm, "end": v(56.5, 65.5) * mm});
            skPoint(sketch, "E3.5.4.1", {"position": v(37.5, 37.5) * mm});
            skLineSegment(sketch, "E3.5.4.2", {"start": v(18.5, 9.5) * mm, "end": v(18.5, 65.5) * mm});
            skCircle(sketch, "E3.5.4.3", {"center": v(37.5, 37.5) * mm, "radius": 37.5 * mm, "construction": true});
            skLineSegment(sketch, "E3.5.4.4", {"start": v(56.5, 9.5) * mm, "end": v(18.5, 9.5) * mm});
            skLineSegment(sketch, "E3.5.4.5", {"start": v(56.5, 65.5) * mm, "end": v(18.5, 65.5) * mm});
            skLineSegment(sketch, "E3.5.5.0", {"start": v(56.5, -65.5) * mm, "end": v(56.5, -9.5) * mm});
            skPoint(sketch, "E3.5.5.1", {"position": v(37.5, -37.5) * mm});
            skLineSegment(sketch, "E3.5.5.2", {"start": v(18.5, -65.5) * mm, "end": v(18.5, -9.5) * mm});
            skCircle(sketch, "E3.5.5.3", {"center": v(37.5, -37.5) * mm, "radius": 37.5 * mm, "construction": true});
            skLineSegment(sketch, "E3.5.5.4", {"start": v(56.5, -65.5) * mm, "end": v(18.5, -65.5) * mm});
            skLineSegment(sketch, "E3.5.5.5", {"start": v(56.5, -9.5) * mm, "end": v(18.5, -9.5) * mm});
            skLineSegment(sketch, "E3.5.6.0", {"start": v(56.5, -140.5) * mm, "end": v(56.5, -84.5) * mm});
            skPoint(sketch, "E3.5.6.1", {"position": v(37.5, -112.5) * mm});
            skLineSegment(sketch, "E3.5.6.2", {"start": v(18.5, -140.5) * mm, "end": v(18.5, -84.5) * mm});
            skCircle(sketch, "E3.5.6.3", {"center": v(37.5, -112.5) * mm, "radius": 37.5 * mm, "construction": true});
            skLineSegment(sketch, "E3.5.6.4", {"start": v(56.5, -140.5) * mm, "end": v(18.5, -140.5) * mm});
            skLineSegment(sketch, "E3.5.6.5", {"start": v(56.5, -84.5) * mm, "end": v(18.5, -84.5) * mm});
            skLineSegment(sketch, "E3.5.7.0", {"start": v(56.5, -215.5) * mm, "end": v(56.5, -159.5) * mm});
            skPoint(sketch, "E3.5.7.1", {"position": v(37.5, -187.5) * mm});
            skLineSegment(sketch, "E3.5.7.2", {"start": v(18.5, -215.5) * mm, "end": v(18.5, -159.5) * mm});
            skCircle(sketch, "E3.5.7.3", {"center": v(37.5, -187.5) * mm, "radius": 37.5 * mm, "construction": true});
            skLineSegment(sketch, "E3.5.7.4", {"start": v(56.5, -215.5) * mm, "end": v(18.5, -215.5) * mm});
            skLineSegment(sketch, "E3.5.7.5", {"start": v(56.5, -159.5) * mm, "end": v(18.5, -159.5) * mm});
            skLineSegment(sketch, "E3.5.8.0", {"start": v(56.5, -290.5) * mm, "end": v(56.5, -234.5) * mm});
            skPoint(sketch, "E3.5.8.1", {"position": v(37.5, -262.5) * mm});
            skLineSegment(sketch, "E3.5.8.2", {"start": v(18.5, -290.5) * mm, "end": v(18.5, -234.5) * mm});
            skCircle(sketch, "E3.5.8.3", {"center": v(37.5, -262.5) * mm, "radius": 37.5 * mm, "construction": true});
            skLineSegment(sketch, "E3.5.8.4", {"start": v(56.5, -290.5) * mm, "end": v(18.5, -290.5) * mm});
            skLineSegment(sketch, "E3.5.8.5", {"start": v(56.5, -234.5) * mm, "end": v(18.5, -234.5) * mm});
            skLineSegment(sketch, "E3.5.9.0", {"start": v(56.5, -365.5) * mm, "end": v(56.5, -309.5) * mm});
            skPoint(sketch, "E3.5.9.1", {"position": v(37.5, -337.5) * mm});
            skLineSegment(sketch, "E3.5.9.2", {"start": v(18.5, -365.5) * mm, "end": v(18.5, -309.5) * mm});
            skCircle(sketch, "E3.5.9.3", {"center": v(37.5, -337.5) * mm, "radius": 37.5 * mm, "construction": true});
            skLineSegment(sketch, "E3.5.9.4", {"start": v(56.5, -365.5) * mm, "end": v(18.5, -365.5) * mm});
            skLineSegment(sketch, "E3.5.9.5", {"start": v(56.5, -309.5) * mm, "end": v(18.5, -309.5) * mm});
            skLineSegment(sketch, "E3.6.0.0", {"start": v(131.5, 309.5) * mm, "end": v(131.5, 365.5) * mm});
            skPoint(sketch, "E3.6.0.1", {"position": v(112.5, 337.5) * mm});
            skLineSegment(sketch, "E3.6.0.2", {"start": v(93.5, 309.5) * mm, "end": v(93.5, 365.5) * mm});
            skCircle(sketch, "E3.6.0.3", {"center": v(112.5, 337.5) * mm, "radius": 37.5 * mm, "construction": true});
            skLineSegment(sketch, "E3.6.0.4", {"start": v(131.5, 309.5) * mm, "end": v(93.5, 309.5) * mm});
            skLineSegment(sketch, "E3.6.0.5", {"start": v(131.5, 365.5) * mm, "end": v(93.5, 365.5) * mm});
            skLineSegment(sketch, "E3.6.1.0", {"start": v(131.5, 234.5) * mm, "end": v(131.5, 290.5) * mm});
            skPoint(sketch, "E3.6.1.1", {"position": v(112.5, 262.5) * mm});
            skLineSegment(sketch, "E3.6.1.2", {"start": v(93.5, 234.5) * mm, "end": v(93.5, 290.5) * mm});
            skCircle(sketch, "E3.6.1.3", {"center": v(112.5, 262.5) * mm, "radius": 37.5 * mm, "construction": true});
            skLineSegment(sketch, "E3.6.1.4", {"start": v(131.5, 234.5) * mm, "end": v(93.5, 234.5) * mm});
            skLineSegment(sketch, "E3.6.1.5", {"start": v(131.5, 290.5) * mm, "end": v(93.5, 290.5) * mm});
            skLineSegment(sketch, "E3.6.2.0", {"start": v(131.5, 159.5) * mm, "end": v(131.5, 215.5) * mm});
            skPoint(sketch, "E3.6.2.1", {"position": v(112.5, 187.5) * mm});
            skLineSegment(sketch, "E3.6.2.2", {"start": v(93.5, 159.5) * mm, "end": v(93.5, 215.5) * mm});
            skCircle(sketch, "E3.6.2.3", {"center": v(112.5, 187.5) * mm, "radius": 37.5 * mm, "construction": true});
            skLineSegment(sketch, "E3.6.2.4", {"start": v(131.5, 159.5) * mm, "end": v(93.5, 159.5) * mm});
            skLineSegment(sketch, "E3.6.2.5", {"start": v(131.5, 215.5) * mm, "end": v(93.5, 215.5) * mm});
            skLineSegment(sketch, "E3.6.3.0", {"start": v(131.5, 84.5) * mm, "end": v(131.5, 140.5) * mm});
            skPoint(sketch, "E3.6.3.1", {"position": v(112.5, 112.5) * mm});
            skLineSegment(sketch, "E3.6.3.2", {"start": v(93.5, 84.5) * mm, "end": v(93.5, 140.5) * mm});
            skCircle(sketch, "E3.6.3.3", {"center": v(112.5, 112.5) * mm, "radius": 37.5 * mm, "construction": true});
            skLineSegment(sketch, "E3.6.3.4", {"start": v(131.5, 84.5) * mm, "end": v(93.5, 84.5) * mm});
            skLineSegment(sketch, "E3.6.3.5", {"start": v(131.5, 140.5) * mm, "end": v(93.5, 140.5) * mm});
            skLineSegment(sketch, "E3.6.4.0", {"start": v(131.5, 9.5) * mm, "end": v(131.5, 65.5) * mm});
            skPoint(sketch, "E3.6.4.1", {"position": v(112.5, 37.5) * mm});
            skLineSegment(sketch, "E3.6.4.2", {"start": v(93.5, 9.5) * mm, "end": v(93.5, 65.5) * mm});
            skCircle(sketch, "E3.6.4.3", {"center": v(112.5, 37.5) * mm, "radius": 37.5 * mm, "construction": true});
            skLineSegment(sketch, "E3.6.4.4", {"start": v(131.5, 9.5) * mm, "end": v(93.5, 9.5) * mm});
            skLineSegment(sketch, "E3.6.4.5", {"start": v(131.5, 65.5) * mm, "end": v(93.5, 65.5) * mm});
            skLineSegment(sketch, "E3.6.5.0", {"start": v(131.5, -65.5) * mm, "end": v(131.5, -9.5) * mm});
            skPoint(sketch, "E3.6.5.1", {"position": v(112.5, -37.5) * mm});
            skLineSegment(sketch, "E3.6.5.2", {"start": v(93.5, -65.5) * mm, "end": v(93.5, -9.5) * mm});
            skCircle(sketch, "E3.6.5.3", {"center": v(112.5, -37.5) * mm, "radius": 37.5 * mm, "construction": true});
            skLineSegment(sketch, "E3.6.5.4", {"start": v(131.5, -65.5) * mm, "end": v(93.5, -65.5) * mm});
            skLineSegment(sketch, "E3.6.5.5", {"start": v(131.5, -9.5) * mm, "end": v(93.5, -9.5) * mm});
            skLineSegment(sketch, "E3.6.6.0", {"start": v(131.5, -140.5) * mm, "end": v(131.5, -84.5) * mm});
            skPoint(sketch, "E3.6.6.1", {"position": v(112.5, -112.5) * mm});
            skLineSegment(sketch, "E3.6.6.2", {"start": v(93.5, -140.5) * mm, "end": v(93.5, -84.5) * mm});
            skCircle(sketch, "E3.6.6.3", {"center": v(112.5, -112.5) * mm, "radius": 37.5 * mm, "construction": true});
            skLineSegment(sketch, "E3.6.6.4", {"start": v(131.5, -140.5) * mm, "end": v(93.5, -140.5) * mm});
            skLineSegment(sketch, "E3.6.6.5", {"start": v(131.5, -84.5) * mm, "end": v(93.5, -84.5) * mm});
            skLineSegment(sketch, "E3.6.7.0", {"start": v(131.5, -215.5) * mm, "end": v(131.5, -159.5) * mm});
            skPoint(sketch, "E3.6.7.1", {"position": v(112.5, -187.5) * mm});
            skLineSegment(sketch, "E3.6.7.2", {"start": v(93.5, -215.5) * mm, "end": v(93.5, -159.5) * mm});
            skCircle(sketch, "E3.6.7.3", {"center": v(112.5, -187.5) * mm, "radius": 37.5 * mm, "construction": true});
            skLineSegment(sketch, "E3.6.7.4", {"start": v(131.5, -215.5) * mm, "end": v(93.5, -215.5) * mm});
            skLineSegment(sketch, "E3.6.7.5", {"start": v(131.5, -159.5) * mm, "end": v(93.5, -159.5) * mm});
            skLineSegment(sketch, "E3.6.8.0", {"start": v(131.5, -290.5) * mm, "end": v(131.5, -234.5) * mm});
            skPoint(sketch, "E3.6.8.1", {"position": v(112.5, -262.5) * mm});
            skLineSegment(sketch, "E3.6.8.2", {"start": v(93.5, -290.5) * mm, "end": v(93.5, -234.5) * mm});
            skCircle(sketch, "E3.6.8.3", {"center": v(112.5, -262.5) * mm, "radius": 37.5 * mm, "construction": true});
            skLineSegment(sketch, "E3.6.8.4", {"start": v(131.5, -290.5) * mm, "end": v(93.5, -290.5) * mm});
            skLineSegment(sketch, "E3.6.8.5", {"start": v(131.5, -234.5) * mm, "end": v(93.5, -234.5) * mm});
            skLineSegment(sketch, "E3.6.9.0", {"start": v(131.5, -365.5) * mm, "end": v(131.5, -309.5) * mm});
            skPoint(sketch, "E3.6.9.1", {"position": v(112.5, -337.5) * mm});
            skLineSegment(sketch, "E3.6.9.2", {"start": v(93.5, -365.5) * mm, "end": v(93.5, -309.5) * mm});
            skCircle(sketch, "E3.6.9.3", {"center": v(112.5, -337.5) * mm, "radius": 37.5 * mm, "construction": true});
            skLineSegment(sketch, "E3.6.9.4", {"start": v(131.5, -365.5) * mm, "end": v(93.5, -365.5) * mm});
            skLineSegment(sketch, "E3.6.9.5", {"start": v(131.5, -309.5) * mm, "end": v(93.5, -309.5) * mm});
            skLineSegment(sketch, "E3.7.0.0", {"start": v(206.5, 309.5) * mm, "end": v(206.5, 365.5) * mm});
            skPoint(sketch, "E3.7.0.1", {"position": v(187.5, 337.5) * mm});
            skLineSegment(sketch, "E3.7.0.2", {"start": v(168.5, 309.5) * mm, "end": v(168.5, 365.5) * mm});
            skCircle(sketch, "E3.7.0.3", {"center": v(187.5, 337.5) * mm, "radius": 37.5 * mm, "construction": true});
            skLineSegment(sketch, "E3.7.0.4", {"start": v(206.5, 309.5) * mm, "end": v(168.5, 309.5) * mm});
            skLineSegment(sketch, "E3.7.0.5", {"start": v(206.5, 365.5) * mm, "end": v(168.5, 365.5) * mm});
            skLineSegment(sketch, "E3.7.1.0", {"start": v(206.5, 234.5) * mm, "end": v(206.5, 290.5) * mm});
            skPoint(sketch, "E3.7.1.1", {"position": v(187.5, 262.5) * mm});
            skLineSegment(sketch, "E3.7.1.2", {"start": v(168.5, 234.5) * mm, "end": v(168.5, 290.5) * mm});
            skCircle(sketch, "E3.7.1.3", {"center": v(187.5, 262.5) * mm, "radius": 37.5 * mm, "construction": true});
            skLineSegment(sketch, "E3.7.1.4", {"start": v(206.5, 234.5) * mm, "end": v(168.5, 234.5) * mm});
            skLineSegment(sketch, "E3.7.1.5", {"start": v(206.5, 290.5) * mm, "end": v(168.5, 290.5) * mm});
            skLineSegment(sketch, "E3.7.2.0", {"start": v(206.5, 159.5) * mm, "end": v(206.5, 215.5) * mm});
            skPoint(sketch, "E3.7.2.1", {"position": v(187.5, 187.5) * mm});
            skLineSegment(sketch, "E3.7.2.2", {"start": v(168.5, 159.5) * mm, "end": v(168.5, 215.5) * mm});
            skCircle(sketch, "E3.7.2.3", {"center": v(187.5, 187.5) * mm, "radius": 37.5 * mm, "construction": true});
            skLineSegment(sketch, "E3.7.2.4", {"start": v(206.5, 159.5) * mm, "end": v(168.5, 159.5) * mm});
            skLineSegment(sketch, "E3.7.2.5", {"start": v(206.5, 215.5) * mm, "end": v(168.5, 215.5) * mm});
            skLineSegment(sketch, "E3.7.3.0", {"start": v(206.5, 84.5) * mm, "end": v(206.5, 140.5) * mm});
            skPoint(sketch, "E3.7.3.1", {"position": v(187.5, 112.5) * mm});
            skLineSegment(sketch, "E3.7.3.2", {"start": v(168.5, 84.5) * mm, "end": v(168.5, 140.5) * mm});
            skCircle(sketch, "E3.7.3.3", {"center": v(187.5, 112.5) * mm, "radius": 37.5 * mm, "construction": true});
            skLineSegment(sketch, "E3.7.3.4", {"start": v(206.5, 84.5) * mm, "end": v(168.5, 84.5) * mm});
            skLineSegment(sketch, "E3.7.3.5", {"start": v(206.5, 140.5) * mm, "end": v(168.5, 140.5) * mm});
            skLineSegment(sketch, "E3.7.4.0", {"start": v(206.5, 9.5) * mm, "end": v(206.5, 65.5) * mm});
            skPoint(sketch, "E3.7.4.1", {"position": v(187.5, 37.5) * mm});
            skLineSegment(sketch, "E3.7.4.2", {"start": v(168.5, 9.5) * mm, "end": v(168.5, 65.5) * mm});
            skCircle(sketch, "E3.7.4.3", {"center": v(187.5, 37.5) * mm, "radius": 37.5 * mm, "construction": true});
            skLineSegment(sketch, "E3.7.4.4", {"start": v(206.5, 9.5) * mm, "end": v(168.5, 9.5) * mm});
            skLineSegment(sketch, "E3.7.4.5", {"start": v(206.5, 65.5) * mm, "end": v(168.5, 65.5) * mm});
            skLineSegment(sketch, "E3.7.5.0", {"start": v(206.5, -65.5) * mm, "end": v(206.5, -9.5) * mm});
            skPoint(sketch, "E3.7.5.1", {"position": v(187.5, -37.5) * mm});
            skLineSegment(sketch, "E3.7.5.2", {"start": v(168.5, -65.5) * mm, "end": v(168.5, -9.5) * mm});
            skCircle(sketch, "E3.7.5.3", {"center": v(187.5, -37.5) * mm, "radius": 37.5 * mm, "construction": true});
            skLineSegment(sketch, "E3.7.5.4", {"start": v(206.5, -65.5) * mm, "end": v(168.5, -65.5) * mm});
            skLineSegment(sketch, "E3.7.5.5", {"start": v(206.5, -9.5) * mm, "end": v(168.5, -9.5) * mm});
            skLineSegment(sketch, "E3.7.6.0", {"start": v(206.5, -140.5) * mm, "end": v(206.5, -84.5) * mm});
            skPoint(sketch, "E3.7.6.1", {"position": v(187.5, -112.5) * mm});
            skLineSegment(sketch, "E3.7.6.2", {"start": v(168.5, -140.5) * mm, "end": v(168.5, -84.5) * mm});
            skCircle(sketch, "E3.7.6.3", {"center": v(187.5, -112.5) * mm, "radius": 37.5 * mm, "construction": true});
            skLineSegment(sketch, "E3.7.6.4", {"start": v(206.5, -140.5) * mm, "end": v(168.5, -140.5) * mm});
            skLineSegment(sketch, "E3.7.6.5", {"start": v(206.5, -84.5) * mm, "end": v(168.5, -84.5) * mm});
            skLineSegment(sketch, "E3.7.7.0", {"start": v(206.5, -215.5) * mm, "end": v(206.5, -159.5) * mm});
            skPoint(sketch, "E3.7.7.1", {"position": v(187.5, -187.5) * mm});
            skLineSegment(sketch, "E3.7.7.2", {"start": v(168.5, -215.5) * mm, "end": v(168.5, -159.5) * mm});
            skCircle(sketch, "E3.7.7.3", {"center": v(187.5, -187.5) * mm, "radius": 37.5 * mm, "construction": true});
            skLineSegment(sketch, "E3.7.7.4", {"start": v(206.5, -215.5) * mm, "end": v(168.5, -215.5) * mm});
            skLineSegment(sketch, "E3.7.7.5", {"start": v(206.5, -159.5) * mm, "end": v(168.5, -159.5) * mm});
            skLineSegment(sketch, "E3.7.8.0", {"start": v(206.5, -290.5) * mm, "end": v(206.5, -234.5) * mm});
            skPoint(sketch, "E3.7.8.1", {"position": v(187.5, -262.5) * mm});
            skLineSegment(sketch, "E3.7.8.2", {"start": v(168.5, -290.5) * mm, "end": v(168.5, -234.5) * mm});
            skCircle(sketch, "E3.7.8.3", {"center": v(187.5, -262.5) * mm, "radius": 37.5 * mm, "construction": true});
            skLineSegment(sketch, "E3.7.8.4", {"start": v(206.5, -290.5) * mm, "end": v(168.5, -290.5) * mm});
            skLineSegment(sketch, "E3.7.8.5", {"start": v(206.5, -234.5) * mm, "end": v(168.5, -234.5) * mm});
            skLineSegment(sketch, "E3.7.9.0", {"start": v(206.5, -365.5) * mm, "end": v(206.5, -309.5) * mm});
            skPoint(sketch, "E3.7.9.1", {"position": v(187.5, -337.5) * mm});
            skLineSegment(sketch, "E3.7.9.2", {"start": v(168.5, -365.5) * mm, "end": v(168.5, -309.5) * mm});
            skCircle(sketch, "E3.7.9.3", {"center": v(187.5, -337.5) * mm, "radius": 37.5 * mm, "construction": true});
            skLineSegment(sketch, "E3.7.9.4", {"start": v(206.5, -365.5) * mm, "end": v(168.5, -365.5) * mm});
            skLineSegment(sketch, "E3.7.9.5", {"start": v(206.5, -309.5) * mm, "end": v(168.5, -309.5) * mm});
            skLineSegment(sketch, "E3.8.0.0", {"start": v(281.5, 309.5) * mm, "end": v(281.5, 365.5) * mm});
            skPoint(sketch, "E3.8.0.1", {"position": v(262.5, 337.5) * mm});
            skLineSegment(sketch, "E3.8.0.2", {"start": v(243.5, 309.5) * mm, "end": v(243.5, 365.5) * mm});
            skCircle(sketch, "E3.8.0.3", {"center": v(262.5, 337.5) * mm, "radius": 37.5 * mm, "construction": true});
            skLineSegment(sketch, "E3.8.0.4", {"start": v(281.5, 309.5) * mm, "end": v(243.5, 309.5) * mm});
            skLineSegment(sketch, "E3.8.0.5", {"start": v(281.5, 365.5) * mm, "end": v(243.5, 365.5) * mm});
            skLineSegment(sketch, "E3.8.1.0", {"start": v(281.5, 234.5) * mm, "end": v(281.5, 290.5) * mm});
            skPoint(sketch, "E3.8.1.1", {"position": v(262.5, 262.5) * mm});
            skLineSegment(sketch, "E3.8.1.2", {"start": v(243.5, 234.5) * mm, "end": v(243.5, 290.5) * mm});
            skCircle(sketch, "E3.8.1.3", {"center": v(262.5, 262.5) * mm, "radius": 37.5 * mm, "construction": true});
            skLineSegment(sketch, "E3.8.1.4", {"start": v(281.5, 234.5) * mm, "end": v(243.5, 234.5) * mm});
            skLineSegment(sketch, "E3.8.1.5", {"start": v(281.5, 290.5) * mm, "end": v(243.5, 290.5) * mm});
            skLineSegment(sketch, "E3.8.2.0", {"start": v(281.5, 159.5) * mm, "end": v(281.5, 215.5) * mm});
            skPoint(sketch, "E3.8.2.1", {"position": v(262.5, 187.5) * mm});
            skLineSegment(sketch, "E3.8.2.2", {"start": v(243.5, 159.5) * mm, "end": v(243.5, 215.5) * mm});
            skCircle(sketch, "E3.8.2.3", {"center": v(262.5, 187.5) * mm, "radius": 37.5 * mm, "construction": true});
            skLineSegment(sketch, "E3.8.2.4", {"start": v(281.5, 159.5) * mm, "end": v(243.5, 159.5) * mm});
            skLineSegment(sketch, "E3.8.2.5", {"start": v(281.5, 215.5) * mm, "end": v(243.5, 215.5) * mm});
            skLineSegment(sketch, "E3.8.3.0", {"start": v(281.5, 84.5) * mm, "end": v(281.5, 140.5) * mm});
            skPoint(sketch, "E3.8.3.1", {"position": v(262.5, 112.5) * mm});
            skLineSegment(sketch, "E3.8.3.2", {"start": v(243.5, 84.5) * mm, "end": v(243.5, 140.5) * mm});
            skCircle(sketch, "E3.8.3.3", {"center": v(262.5, 112.5) * mm, "radius": 37.5 * mm, "construction": true});
            skLineSegment(sketch, "E3.8.3.4", {"start": v(281.5, 84.5) * mm, "end": v(243.5, 84.5) * mm});
            skLineSegment(sketch, "E3.8.3.5", {"start": v(281.5, 140.5) * mm, "end": v(243.5, 140.5) * mm});
            skLineSegment(sketch, "E3.8.4.0", {"start": v(281.5, 9.5) * mm, "end": v(281.5, 65.5) * mm});
            skPoint(sketch, "E3.8.4.1", {"position": v(262.5, 37.5) * mm});
            skLineSegment(sketch, "E3.8.4.2", {"start": v(243.5, 9.5) * mm, "end": v(243.5, 65.5) * mm});
            skCircle(sketch, "E3.8.4.3", {"center": v(262.5, 37.5) * mm, "radius": 37.5 * mm, "construction": true});
            skLineSegment(sketch, "E3.8.4.4", {"start": v(281.5, 9.5) * mm, "end": v(243.5, 9.5) * mm});
            skLineSegment(sketch, "E3.8.4.5", {"start": v(281.5, 65.5) * mm, "end": v(243.5, 65.5) * mm});
            skLineSegment(sketch, "E3.8.5.0", {"start": v(281.5, -65.5) * mm, "end": v(281.5, -9.5) * mm});
            skPoint(sketch, "E3.8.5.1", {"position": v(262.5, -37.5) * mm});
            skLineSegment(sketch, "E3.8.5.2", {"start": v(243.5, -65.5) * mm, "end": v(243.5, -9.5) * mm});
            skCircle(sketch, "E3.8.5.3", {"center": v(262.5, -37.5) * mm, "radius": 37.5 * mm, "construction": true});
            skLineSegment(sketch, "E3.8.5.4", {"start": v(281.5, -65.5) * mm, "end": v(243.5, -65.5) * mm});
            skLineSegment(sketch, "E3.8.5.5", {"start": v(281.5, -9.5) * mm, "end": v(243.5, -9.5) * mm});
            skLineSegment(sketch, "E3.8.6.0", {"start": v(281.5, -140.5) * mm, "end": v(281.5, -84.5) * mm});
            skPoint(sketch, "E3.8.6.1", {"position": v(262.5, -112.5) * mm});
            skLineSegment(sketch, "E3.8.6.2", {"start": v(243.5, -140.5) * mm, "end": v(243.5, -84.5) * mm});
            skCircle(sketch, "E3.8.6.3", {"center": v(262.5, -112.5) * mm, "radius": 37.5 * mm, "construction": true});
            skLineSegment(sketch, "E3.8.6.4", {"start": v(281.5, -140.5) * mm, "end": v(243.5, -140.5) * mm});
            skLineSegment(sketch, "E3.8.6.5", {"start": v(281.5, -84.5) * mm, "end": v(243.5, -84.5) * mm});
            skLineSegment(sketch, "E3.8.7.0", {"start": v(281.5, -215.5) * mm, "end": v(281.5, -159.5) * mm});
            skPoint(sketch, "E3.8.7.1", {"position": v(262.5, -187.5) * mm});
            skLineSegment(sketch, "E3.8.7.2", {"start": v(243.5, -215.5) * mm, "end": v(243.5, -159.5) * mm});
            skCircle(sketch, "E3.8.7.3", {"center": v(262.5, -187.5) * mm, "radius": 37.5 * mm, "construction": true});
            skLineSegment(sketch, "E3.8.7.4", {"start": v(281.5, -215.5) * mm, "end": v(243.5, -215.5) * mm});
            skLineSegment(sketch, "E3.8.7.5", {"start": v(281.5, -159.5) * mm, "end": v(243.5, -159.5) * mm});
            skLineSegment(sketch, "E3.8.8.0", {"start": v(281.5, -290.5) * mm, "end": v(281.5, -234.5) * mm});
            skPoint(sketch, "E3.8.8.1", {"position": v(262.5, -262.5) * mm});
            skLineSegment(sketch, "E3.8.8.2", {"start": v(243.5, -290.5) * mm, "end": v(243.5, -234.5) * mm});
            skCircle(sketch, "E3.8.8.3", {"center": v(262.5, -262.5) * mm, "radius": 37.5 * mm, "construction": true});
            skLineSegment(sketch, "E3.8.8.4", {"start": v(281.5, -290.5) * mm, "end": v(243.5, -290.5) * mm});
            skLineSegment(sketch, "E3.8.8.5", {"start": v(281.5, -234.5) * mm, "end": v(243.5, -234.5) * mm});
            skLineSegment(sketch, "E3.8.9.0", {"start": v(281.5, -365.5) * mm, "end": v(281.5, -309.5) * mm});
            skPoint(sketch, "E3.8.9.1", {"position": v(262.5, -337.5) * mm});
            skLineSegment(sketch, "E3.8.9.2", {"start": v(243.5, -365.5) * mm, "end": v(243.5, -309.5) * mm});
            skCircle(sketch, "E3.8.9.3", {"center": v(262.5, -337.5) * mm, "radius": 37.5 * mm, "construction": true});
            skLineSegment(sketch, "E3.8.9.4", {"start": v(281.5, -365.5) * mm, "end": v(243.5, -365.5) * mm});
            skLineSegment(sketch, "E3.8.9.5", {"start": v(281.5, -309.5) * mm, "end": v(243.5, -309.5) * mm});
            skLineSegment(sketch, "E3.9.0.0", {"start": v(356.5, 309.5) * mm, "end": v(356.5, 365.5) * mm});
            skPoint(sketch, "E3.9.0.1", {"position": v(337.5, 337.5) * mm});
            skLineSegment(sketch, "E3.9.0.2", {"start": v(318.5, 309.5) * mm, "end": v(318.5, 365.5) * mm});
            skCircle(sketch, "E3.9.0.3", {"center": v(337.5, 337.5) * mm, "radius": 37.5 * mm, "construction": true});
            skLineSegment(sketch, "E3.9.0.4", {"start": v(356.5, 309.5) * mm, "end": v(318.5, 309.5) * mm});
            skLineSegment(sketch, "E3.9.0.5", {"start": v(356.5, 365.5) * mm, "end": v(318.5, 365.5) * mm});
            skLineSegment(sketch, "E3.9.1.0", {"start": v(356.5, 234.5) * mm, "end": v(356.5, 290.5) * mm});
            skPoint(sketch, "E3.9.1.1", {"position": v(337.5, 262.5) * mm});
            skLineSegment(sketch, "E3.9.1.2", {"start": v(318.5, 234.5) * mm, "end": v(318.5, 290.5) * mm});
            skCircle(sketch, "E3.9.1.3", {"center": v(337.5, 262.5) * mm, "radius": 37.5 * mm, "construction": true});
            skLineSegment(sketch, "E3.9.1.4", {"start": v(356.5, 234.5) * mm, "end": v(318.5, 234.5) * mm});
            skLineSegment(sketch, "E3.9.1.5", {"start": v(356.5, 290.5) * mm, "end": v(318.5, 290.5) * mm});
            skLineSegment(sketch, "E3.9.2.0", {"start": v(356.5, 159.5) * mm, "end": v(356.5, 215.5) * mm});
            skPoint(sketch, "E3.9.2.1", {"position": v(337.5, 187.5) * mm});
            skLineSegment(sketch, "E3.9.2.2", {"start": v(318.5, 159.5) * mm, "end": v(318.5, 215.5) * mm});
            skCircle(sketch, "E3.9.2.3", {"center": v(337.5, 187.5) * mm, "radius": 37.5 * mm, "construction": true});
            skLineSegment(sketch, "E3.9.2.4", {"start": v(356.5, 159.5) * mm, "end": v(318.5, 159.5) * mm});
            skLineSegment(sketch, "E3.9.2.5", {"start": v(356.5, 215.5) * mm, "end": v(318.5, 215.5) * mm});
            skLineSegment(sketch, "E3.9.3.0", {"start": v(356.5, 84.5) * mm, "end": v(356.5, 140.5) * mm});
            skPoint(sketch, "E3.9.3.1", {"position": v(337.5, 112.5) * mm});
            skLineSegment(sketch, "E3.9.3.2", {"start": v(318.5, 84.5) * mm, "end": v(318.5, 140.5) * mm});
            skCircle(sketch, "E3.9.3.3", {"center": v(337.5, 112.5) * mm, "radius": 37.5 * mm, "construction": true});
            skLineSegment(sketch, "E3.9.3.4", {"start": v(356.5, 84.5) * mm, "end": v(318.5, 84.5) * mm});
            skLineSegment(sketch, "E3.9.3.5", {"start": v(356.5, 140.5) * mm, "end": v(318.5, 140.5) * mm});
            skLineSegment(sketch, "E3.9.4.0", {"start": v(356.5, 9.5) * mm, "end": v(356.5, 65.5) * mm});
            skPoint(sketch, "E3.9.4.1", {"position": v(337.5, 37.5) * mm});
            skLineSegment(sketch, "E3.9.4.2", {"start": v(318.5, 9.5) * mm, "end": v(318.5, 65.5) * mm});
            skCircle(sketch, "E3.9.4.3", {"center": v(337.5, 37.5) * mm, "radius": 37.5 * mm, "construction": true});
            skLineSegment(sketch, "E3.9.4.4", {"start": v(356.5, 9.5) * mm, "end": v(318.5, 9.5) * mm});
            skLineSegment(sketch, "E3.9.4.5", {"start": v(356.5, 65.5) * mm, "end": v(318.5, 65.5) * mm});
            skLineSegment(sketch, "E3.9.5.0", {"start": v(356.5, -65.5) * mm, "end": v(356.5, -9.5) * mm});
            skPoint(sketch, "E3.9.5.1", {"position": v(337.5, -37.5) * mm});
            skLineSegment(sketch, "E3.9.5.2", {"start": v(318.5, -65.5) * mm, "end": v(318.5, -9.5) * mm});
            skCircle(sketch, "E3.9.5.3", {"center": v(337.5, -37.5) * mm, "radius": 37.5 * mm, "construction": true});
            skLineSegment(sketch, "E3.9.5.4", {"start": v(356.5, -65.5) * mm, "end": v(318.5, -65.5) * mm});
            skLineSegment(sketch, "E3.9.5.5", {"start": v(356.5, -9.5) * mm, "end": v(318.5, -9.5) * mm});
            skLineSegment(sketch, "E3.9.6.0", {"start": v(356.5, -140.5) * mm, "end": v(356.5, -84.5) * mm});
            skPoint(sketch, "E3.9.6.1", {"position": v(337.5, -112.5) * mm});
            skLineSegment(sketch, "E3.9.6.2", {"start": v(318.5, -140.5) * mm, "end": v(318.5, -84.5) * mm});
            skCircle(sketch, "E3.9.6.3", {"center": v(337.5, -112.5) * mm, "radius": 37.5 * mm, "construction": true});
            skLineSegment(sketch, "E3.9.6.4", {"start": v(356.5, -140.5) * mm, "end": v(318.5, -140.5) * mm});
            skLineSegment(sketch, "E3.9.6.5", {"start": v(356.5, -84.5) * mm, "end": v(318.5, -84.5) * mm});
            skLineSegment(sketch, "E3.9.7.0", {"start": v(356.5, -215.5) * mm, "end": v(356.5, -159.5) * mm});
            skPoint(sketch, "E3.9.7.1", {"position": v(337.5, -187.5) * mm});
            skLineSegment(sketch, "E3.9.7.2", {"start": v(318.5, -215.5) * mm, "end": v(318.5, -159.5) * mm});
            skCircle(sketch, "E3.9.7.3", {"center": v(337.5, -187.5) * mm, "radius": 37.5 * mm, "construction": true});
            skLineSegment(sketch, "E3.9.7.4", {"start": v(356.5, -215.5) * mm, "end": v(318.5, -215.5) * mm});
            skLineSegment(sketch, "E3.9.7.5", {"start": v(356.5, -159.5) * mm, "end": v(318.5, -159.5) * mm});
            skLineSegment(sketch, "E3.9.8.0", {"start": v(356.5, -290.5) * mm, "end": v(356.5, -234.5) * mm});
            skPoint(sketch, "E3.9.8.1", {"position": v(337.5, -262.5) * mm});
            skLineSegment(sketch, "E3.9.8.2", {"start": v(318.5, -290.5) * mm, "end": v(318.5, -234.5) * mm});
            skCircle(sketch, "E3.9.8.3", {"center": v(337.5, -262.5) * mm, "radius": 37.5 * mm, "construction": true});
            skLineSegment(sketch, "E3.9.8.4", {"start": v(356.5, -290.5) * mm, "end": v(318.5, -290.5) * mm});
            skLineSegment(sketch, "E3.9.8.5", {"start": v(356.5, -234.5) * mm, "end": v(318.5, -234.5) * mm});
            skLineSegment(sketch, "E3.9.9.0", {"start": v(356.5, -365.5) * mm, "end": v(356.5, -309.5) * mm});
            skPoint(sketch, "E3.9.9.1", {"position": v(337.5, -337.5) * mm});
            skLineSegment(sketch, "E3.9.9.2", {"start": v(318.5, -365.5) * mm, "end": v(318.5, -309.5) * mm});
            skCircle(sketch, "E3.9.9.3", {"center": v(337.5, -337.5) * mm, "radius": 37.5 * mm, "construction": true});
            skLineSegment(sketch, "E3.9.9.4", {"start": v(356.5, -365.5) * mm, "end": v(318.5, -365.5) * mm});
            skLineSegment(sketch, "E3.9.9.5", {"start": v(356.5, -309.5) * mm, "end": v(318.5, -309.5) * mm});
            skLineSegment(sketch, "E3.direction1", {"start": v(-356.5, 309.5) * mm, "end": v(-281.5, 309.5) * mm, "construction": true});
            skLineSegment(sketch, "E3.direction2", {"start": v(-356.5, 309.5) * mm, "end": v(-356.5, 234.5) * mm, "construction": true});
            skSolve(sketch);
        }
        {
            var Q0;
            Q0=qSketchRegion(id+"F2",true);
            extrude(context, id + "F3", {"entities" : qUnion([Q0]), "operationType" : NewBodyOperationType.REMOVE, "oppositeDirection" : true, "depth" : 4 * mm});
        }
    });
